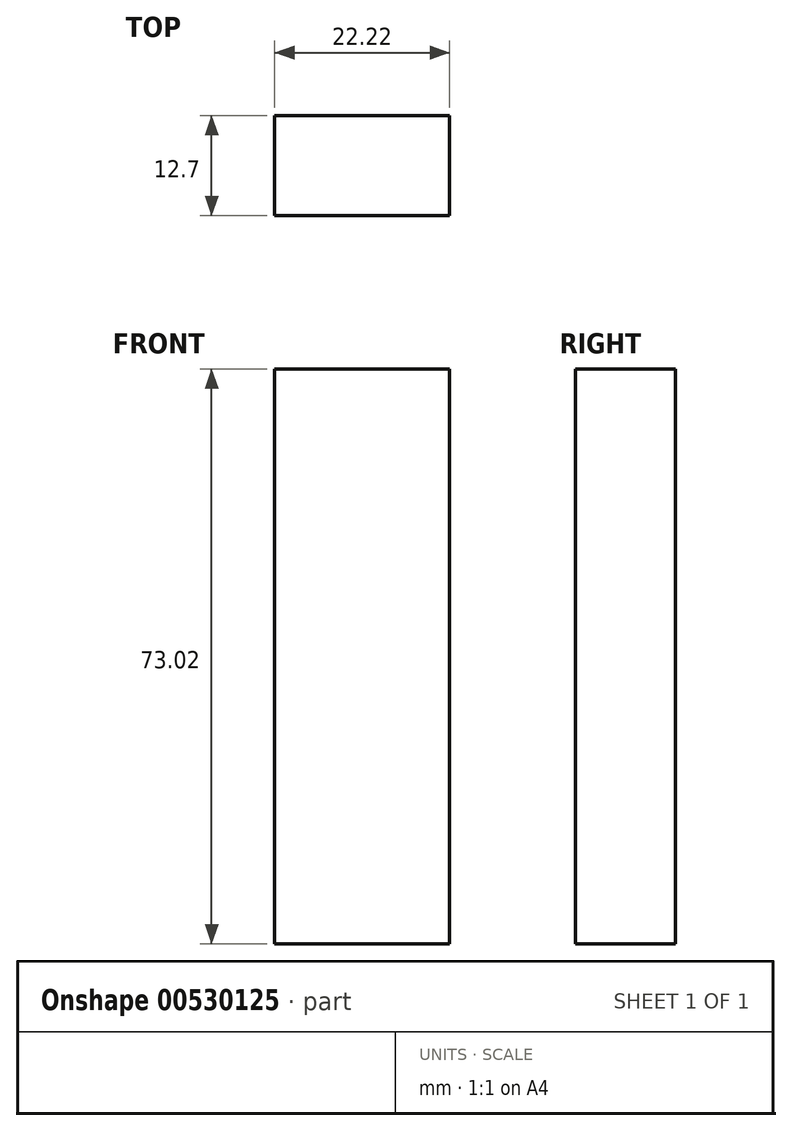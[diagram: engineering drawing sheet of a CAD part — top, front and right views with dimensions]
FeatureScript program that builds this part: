
annotation { "Feature Type Name" : "Feature", "Feature Type Description" : "" }
export const myFeature = defineFeature(function(context is Context, id is Id, definition is map)
    precondition{}
    {
        {
            var Q0;
            Q0=qCreatedBy(makeId("Front.planeOp"),FACE);
            var sketch = newSketch(context, id + "F0", { "sketchPlane" : qUnion([Q0])});
            skLineSegment(sketch, "E0.bottom", {"start": v(-18.18, 39.01) * mm, "end": v(4.04, 39.01) * mm});
            skLineSegment(sketch, "E0.top", {"start": v(-18.18, -34.01) * mm, "end": v(4.04, -34.01) * mm});
            skLineSegment(sketch, "E0.left", {"start": v(-18.18, 39.01) * mm, "end": v(-18.18, -34.01) * mm});
            skLineSegment(sketch, "E0.right", {"start": v(4.04, 39.01) * mm, "end": v(4.04, -34.01) * mm});
            skSolve(sketch);
        }
        {
            var Q0;
            Q0 = qSketchRegion(id + "F0", true);
            extrude(context, id + "F1", {"entities" : qUnion([Q0]), "depth" : 12.7 * mm, "offsetDistance" : 25.4 * mm});
        }
    });
